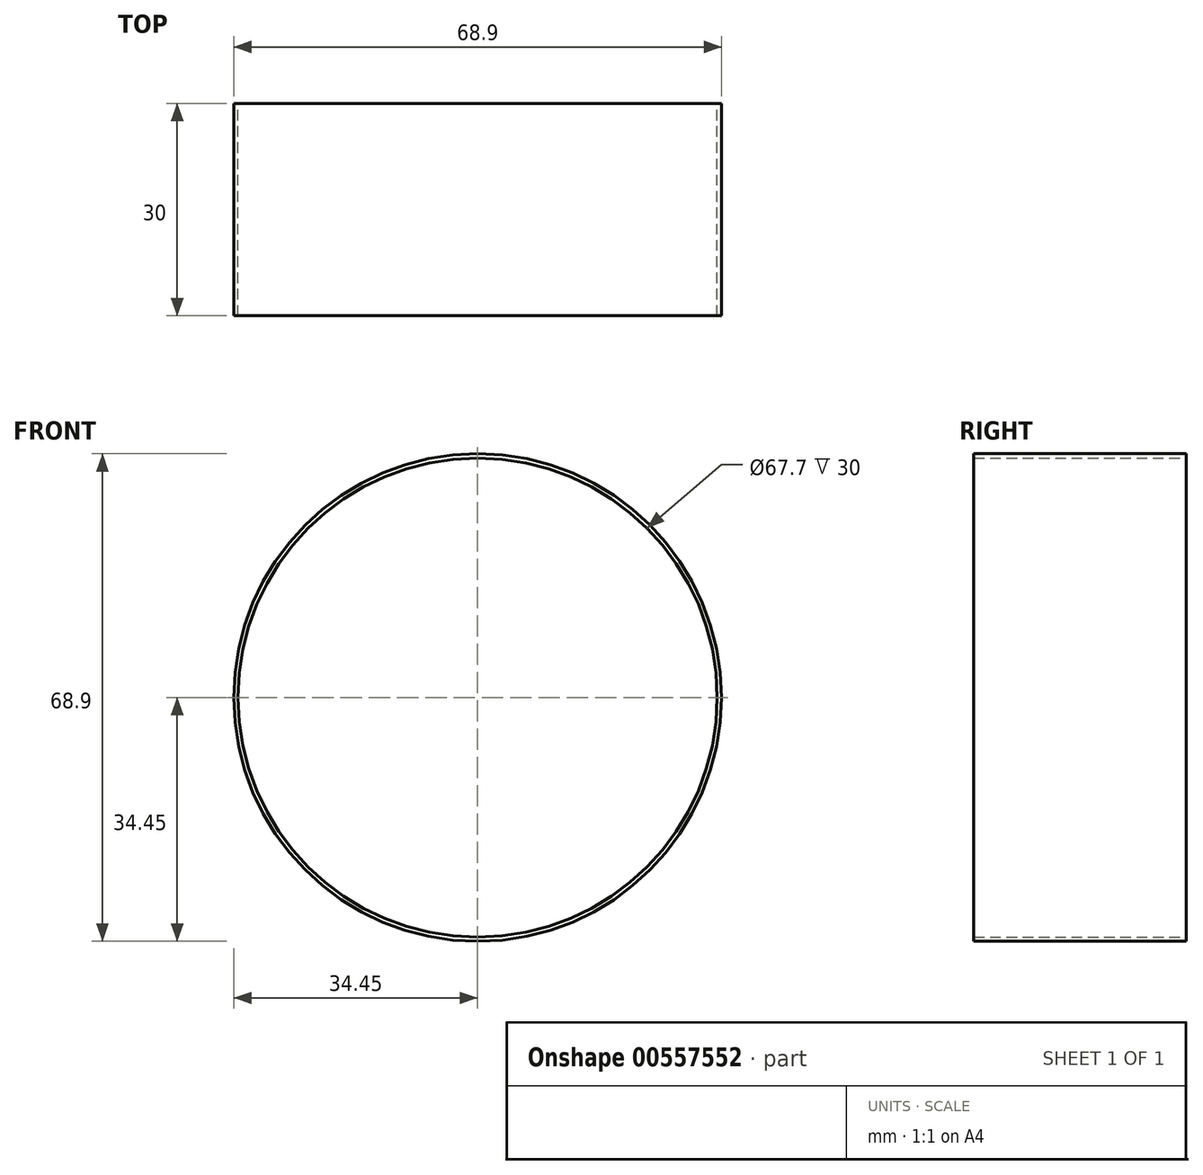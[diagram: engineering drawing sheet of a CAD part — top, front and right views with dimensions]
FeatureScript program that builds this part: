
annotation { "Feature Type Name" : "Feature", "Feature Type Description" : "" }
export const myFeature = defineFeature(function(context is Context, id is Id, definition is map)
    precondition{}
    {
        {
            var Q0;
            Q0=qCreatedBy(makeId("Front.planeOp"),FACE);
            var sketch = newSketch(context, id + "F0", { "sketchPlane" : qUnion([Q0])});
            skCircle(sketch, "E0", {"center": v(0, 0) * mm, "radius": 33.85 * mm});
            skCircle(sketch, "E1.0", {"center": v(0, 0) * mm, "radius": 34.45 * mm});
            skSolve(sketch);
        }
        {
            var Q0;
            Q0=makeQuery(id+"F0.imprint","IMPRINT",FACE,{"disambiguationData":[TD([[makeQuery(id+"F0.imprint","IMPRINT",EDGE,{"derivedFrom":sQuery(id+"F0.wireOp",EDGE,"E0")}),-1.0]])]});
            var Q1;
            Q1=sQuery(id+"F0.wireOp",EDGE,"E0");
            extrude(context, id + "F1", {"entities" : qUnion([Q0]), "surfaceEntities" : qUnion([Q1]), "depth" : 30 * mm, "offsetDistance" : 25 * mm});
        }
    });
